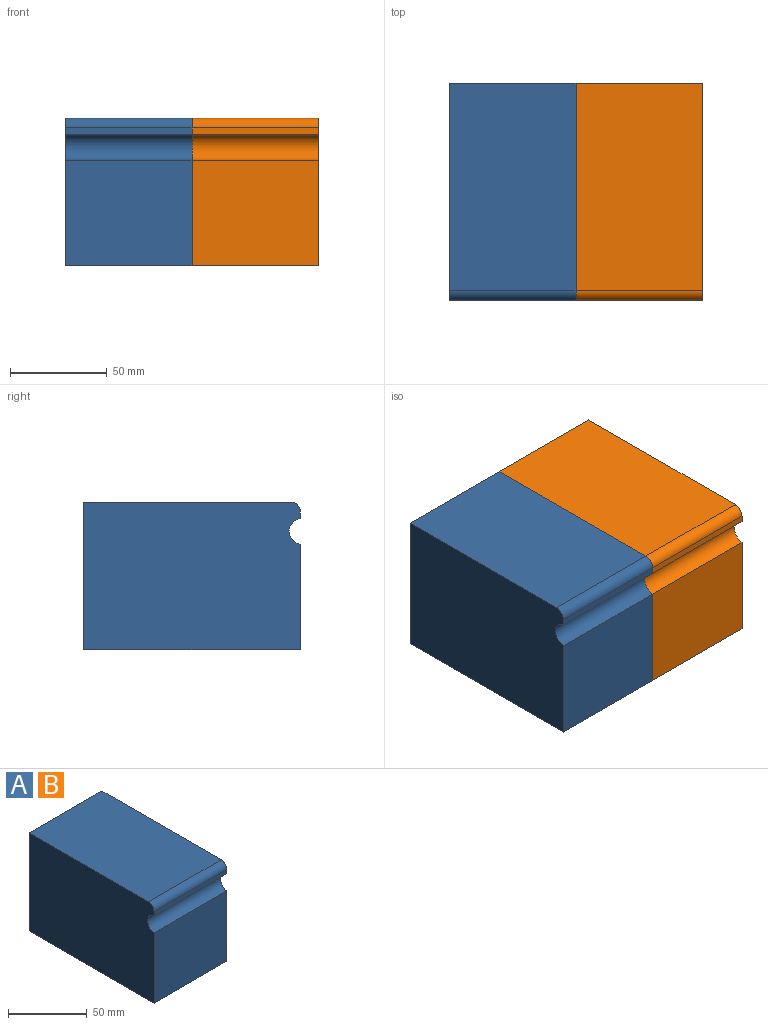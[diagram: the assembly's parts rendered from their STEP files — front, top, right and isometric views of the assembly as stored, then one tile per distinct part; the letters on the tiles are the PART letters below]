
ASSEMBLY  parts=2 mates=1
PART A: 9 faces, bbox 65.3x112x76.2 mm
  f0: plane 65.3x3.38mm, normal (0,-1,0), area 220.4mm2, adj f5,f6,f7,f8
  f1: plane 107x65.3mm, normal (0,0,1), area 6987.1mm2, adj f4,f5,f6,f8
  f2: plane 65.3x54.58mm, normal (0,-1,0), area 3563.8mm2, adj f3,f5,f6,f7
  f3: plane 112x65.3mm, normal (0,0,-1), area 7313.6mm2, adj f2,f4,f5,f6
  f4: plane 76.2x65.3mm, normal (0,1,0), area 4975.9mm2, adj f1,f3,f5,f6
  f5: plane 112x76.2mm, normal (1,0,0), area 8471.9mm2, adj f0,f1,f2,f3,f4,f7,f8
  f6: plane 112x76.2mm, normal (-1,0,0), area 8471.9mm2, adj f0,f1,f2,f3,f4,f7,f8
  f7: cylinder r=6.7mm len=65.3mm, axis (1,0,0), area 1243.4mm2, adj f0,f2,f5,f6
  f8: cylinder r=5mm len=65.3mm, axis (1,0,0), area 512.9mm2, adj f0,f1,f5,f6
PART B: same geometry as A
PLACE A at identity fixed
PLACE B t=(65.3,0,0)mm
MATE fastened A.f5 <-> B.f6  axis (1,0,0) through (65.3,15.65,-27.31)mm
